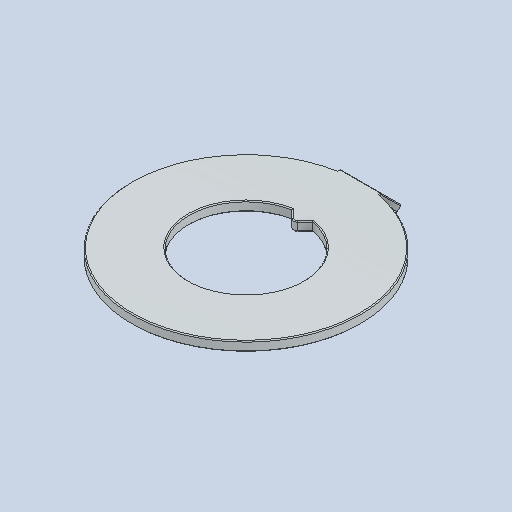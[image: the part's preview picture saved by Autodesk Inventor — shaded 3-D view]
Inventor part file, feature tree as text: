
AUTODESK INVENTOR PART (.ipt)
format: ipt  version: 2025.1 (Build 291241020, 241B)  size: 160,768 bytes
history: native  units: in
note: dims shown in document units (in); Inventor stores cm internally (conversion verified against a paired STEP export)
features: fillet x1
ambient origin geometry x8: Origin, YZ Plane, XZ Plane, XY Plane, X Axis, Y Axis, Z Axis, Center Point
bodies: Solid1 (feature_tree)
feature tree (1):
  fillet  "Fillet4"  [1 undecoded]
note: 1 required parameter value undecoded (feature->parameter linkage not recoverable at this tier; creation-order binding heuristic only, values carry confidence <= 0.55)
